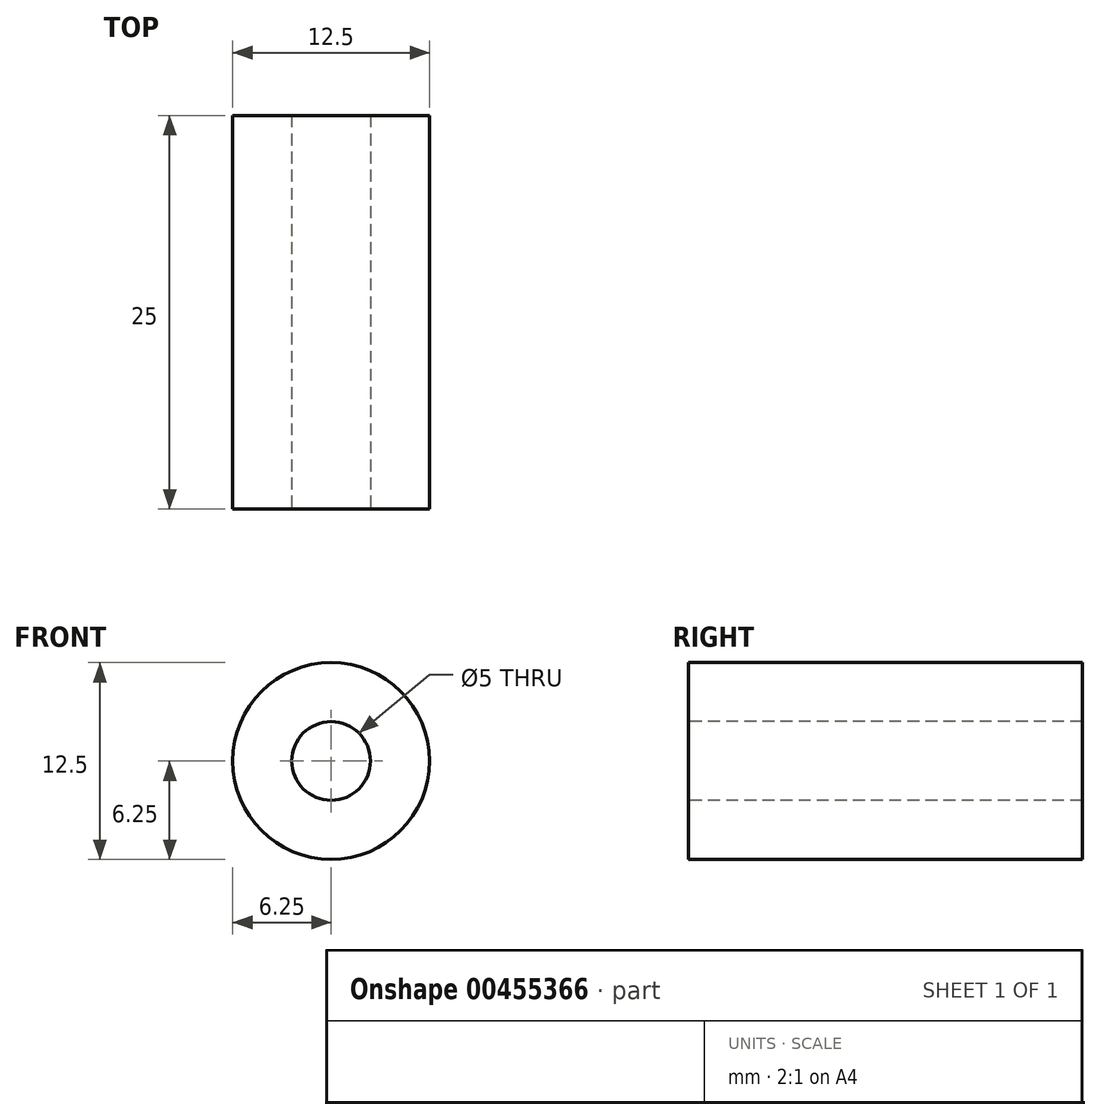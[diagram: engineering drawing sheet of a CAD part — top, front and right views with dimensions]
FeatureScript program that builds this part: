
annotation { "Feature Type Name" : "Feature", "Feature Type Description" : "" }
export const myFeature = defineFeature(function(context is Context, id is Id, definition is map)
    precondition{}
    {
        {
            var Q0;
            Q0=qCreatedBy(makeId("Front.planeOp"),FACE);
            var sketch = newSketch(context, id + "F0", { "sketchPlane" : qUnion([Q0])});
            skCircle(sketch, "E0", {"center": v(0, 0) * mm, "radius": 6.25 * mm});
            skSolve(sketch);
        }
        {
            var Q0;
            Q0 = qSketchRegion(id + "F0", true);
            extrude(context, id + "F1", {"entities" : qUnion([Q0]), "depth" : 25 * mm});
        }
        {
            var Q0;
            Q0=makeQuery(id+"F1.opExtrude","CAP_FACE",FACE,{"disambiguationData":[OSD([sQuery(id+"F0.wireOp",EDGE,"E0")])],"isStart":false});
            var sketch = newSketch(context, id + "F2", { "sketchPlane" : qUnion([Q0])});
            skPoint(sketch, "E1", {"position": v(0, 0) * mm});
            skSolve(sketch);
        }
        {
            var Q0;
            Q0=sQuery(id+"F2.wireOp",VERTEX,"E1");
            var Q1;
            Q1=makeQuery(id+"F1.opExtrude","SWEPT_BODY",BODY,{"disambiguationData":[OSD([sQuery(id+"F0.wireOp",EDGE,"E0")])]});
            hole(context, id + "F3", {"style" : HoleStyle.SIMPLE, "endStyle" : HoleEndStyle.BLIND, "holeDiameter" : 5 * mm, "holeDepth" : 37.5 * mm, "isTappedThrough" : true, "tappedDepth" : 12 * mm, "tapClearance" : 3, "locations" : qUnion([Q0]), "scope" : qUnion([Q1])});
        }
    });
